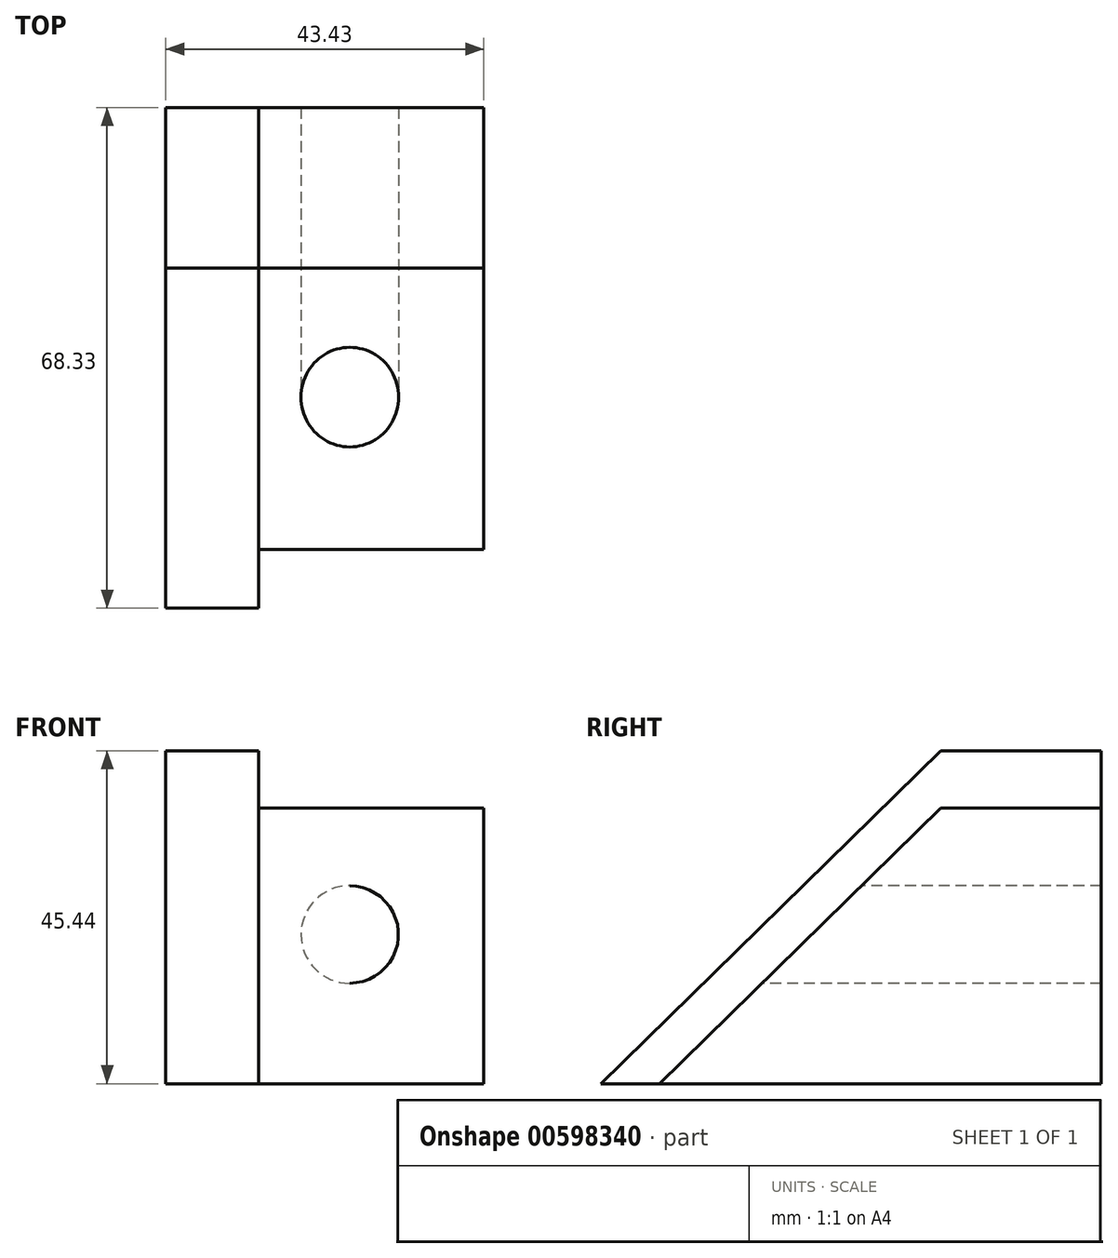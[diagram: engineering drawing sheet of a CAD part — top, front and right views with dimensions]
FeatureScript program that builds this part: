
annotation { "Feature Type Name" : "Feature", "Feature Type Description" : "" }
export const myFeature = defineFeature(function(context is Context, id is Id, definition is map)
    precondition{}
    {
        {
            var Q0;
            Q0=qCreatedBy(makeId("Right.planeOp"),FACE);
            var sketch = newSketch(context, id + "F0", { "sketchPlane" : qUnion([Q0])});
            skLineSegment(sketch, "E0", {"start": v(31.83, 0) * mm, "end": v(31.83, 37.6) * mm});
            skLineSegment(sketch, "E1", {"start": v(31.83, 37.6) * mm, "end": v(9.9, 37.6) * mm});
            skLineSegment(sketch, "E2", {"start": v(9.9, 37.6) * mm, "end": v(-28.5, 0) * mm});
            skLineSegment(sketch, "E3", {"start": v(-28.5, 0) * mm, "end": v(31.83, 0) * mm});
            skLineSegment(sketch, "E4", {"start": v(31.83, 0) * mm, "end": v(31.83, 45.44) * mm});
            skPoint(sketch, "E4.endSnap0", {"position": v(31.83, 18.8) * mm});
            skLineSegment(sketch, "E5", {"start": v(31.83, 45.44) * mm, "end": v(9.9, 45.44) * mm});
            skLineSegment(sketch, "E6", {"start": v(9.9, 45.44) * mm, "end": v(-36.5, 0) * mm});
            skLineSegment(sketch, "E7", {"start": v(-36.5, 0) * mm, "end": v(31.83, 0) * mm});
            skSolve(sketch);
        }
        {
            var Q0;
            {var subQ0=sQuery(id+"F0.wireOp",EDGE,"E1");Q0=makeQuery(id+"F0.imprint","IMPRINT",FACE,{"disambiguationData":[TD([[makeQuery(id+"F0.imprint","IMPRINT",EDGE,{"derivedFrom":subQ0}),1.0]])]});}
            extrude(context, id + "F1", {"entities" : qUnion([Q0]), "depth" : 30.73 * mm, "offsetDistance" : 25.4 * mm});
        }
        {
            var Q0;
            Q0 = qSketchRegion(id + "F0", true);
            var Q1;
            Q1 = qSketchRegion(id + "F3", true);
            extrude(context, id + "F2", {"entities" : qUnion([Q0, Q1]), "operationType" : NewBodyOperationType.ADD, "oppositeDirection" : true, "depth" : 12.7 * mm, "offsetDistance" : 25.4 * mm});
        }
        {
            var Q0;
            Q0=qCreatedBy(makeId("Front.planeOp"),FACE);
            var sketch = newSketch(context, id + "F3", { "sketchPlane" : qUnion([Q0])});
            skCircle(sketch, "E8", {"center": v(12.44, 20.37) * mm, "radius": 6.67 * mm});
            skSolve(sketch);
        }
        {
            var Q0;
            Q0 = qSketchRegion(id + "F3", true);
            extrude(context, id + "F4", {"entities" : qUnion([Q0]), "operationType" : NewBodyOperationType.REMOVE, "oppositeDirection" : true, "depth" : 45.2 * mm, "offsetDistance" : 25.4 * mm});
        }
        {
            var Q0;
            Q0 = qSketchRegion(id + "F3", true);
            extrude(context, id + "F5", {"entities" : qUnion([Q0]), "operationType" : NewBodyOperationType.REMOVE, "depth" : 29.97 * mm, "offsetDistance" : 25.4 * mm});
        }
    });
